# Revit family: VOC3_63_UN_Surface-mounted_ETK
name_source: partatom
category: Lighting Fixtures
revit_build: Autodesk Revit 2017 (Build: 20190508_0315(x64)
units: mm (PartAtom-declared; Revit-internal decimal feet)

## family parameters
Always vertical = No
Cut with Voids When Loaded = No
Light Source = No
OmniClass Number = 23.80.70.00
OmniClass Title = Lighting
Part Type = Normal
Room Calculation Point = Yes
Round Connector Dimension = Use Diameter
Shared = No
Work Plane-Based = No

## types (6) — shared parameters
Assembly Code = 63.0
Description = Surface-mounted luminaire
IfcExportAs = IfcLightFixtureType
IfcExportType = USERDEFINED
Lamp = LED
Luminaire_Body_Material = PPS Plastic
Luminaire_Cap_Material = PPS Plastic
Manufacturer = ETK licht B.V.
Model = VOC.3
URL = https://www.etk.nl
Voltage = 230 V

## per-type parameters (varying)
| type | Apparent Load | Geometry | Lightsource | Wattage Comments |
| VOC.3100.20 - 12W / 1300lm / 4000K | 12 VA | VOC3 - Geometry : VOC.3100.20 - 12W / 1300lm / 4000K | VOC.3 - Lightsource : VOC.3100.20 - 12W / 1300lm / 4000K | 12W |
| VOC.3200.20 - 23W / 2600lm / 4000K | 23 VA | VOC3 - Geometry : VOC.3200.20 - 23W / 2600lm / 4000K | VOC.3 - Lightsource : VOC.3200.20 - 23W / 2600lm / 4000K | 23W |
| VOC.3300.20 - 24W / 2700lm / 4000K | 24 VA | VOC3 - Geometry : VOC.3300.20 - 24W / 2700lm / 4000K | VOC.3 - Lightsource : VOC.3300.20 - 24W / 2700lm / 4000K | 24W |
| VOC.3400.20 - 47W / 5300lm / 4000K | 47 VA | VOC3 - Geometry : VOC.3400.20 - 47W / 5300lm / 4000K | VOC.3 - Lightsource : VOC.3400.20 - 47W / 5300lm / 4000K | 47W |
| VOC.3500.20 - 26W / 3000lm / 4000K | 26 VA | VOC3 - Geometry : VOC.3500.20 - 26W / 3000lm / 4000K | VOC.3 - Lightsource : VOC.3500.20 - 26W / 3000lm / 4000K | 26W |
| VOC.3600.20 - 52W / 5800lm / 4000K | 52 VA | VOC3 - Geometry : VOC.3600.20 - 52W / 5800lm / 4000K | VOC.3 - Lightsource : VOC.3600.20 - 52W / 5800lm / 4000K | 52W |

## geometry (parser evidence)
native form markers: Sweep x8
no freeform markers — native parametric forms only
